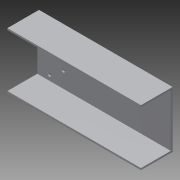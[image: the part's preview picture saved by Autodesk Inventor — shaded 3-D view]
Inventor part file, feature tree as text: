
AUTODESK INVENTOR PART (.ipt)
format: ipt  version: 2013 (Build 170138000, 138)  size: 97,280 bytes
history: native  units: in
note: dims shown in document units (in); Inventor stores cm internally (conversion verified against a paired STEP export)
features: other x4, reference x2, hole x1, sketch x1
ambient origin geometry x8: Origin, YZ Plane, XZ Plane, XY Plane, X Axis, Y Axis, Z Axis, Center Point
bodies: Solid1 (feature_tree)
feature tree (8):
  other  "Table"
  other  "channel2.25x4.ipt"
  hole  "Hole1"  [1 undecoded]
  other  "Solid1::channel2.25x4.ipt"
  other  "TaggingFeature1"
  sketch  "Sketch1"  dims[d0=4.0in d1=2.25in d2=0.125in d4=0.0in d3=0.26in d5=0.75in d6=0.375in d7=0.25in d8=0.5635in d9=1.0in d10=0.8108in]
  reference  "Reference1"
  reference  "Reference2"
note: 1 required parameter value undecoded (feature->parameter linkage not recoverable at this tier; creation-order binding heuristic only, values carry confidence <= 0.55)
